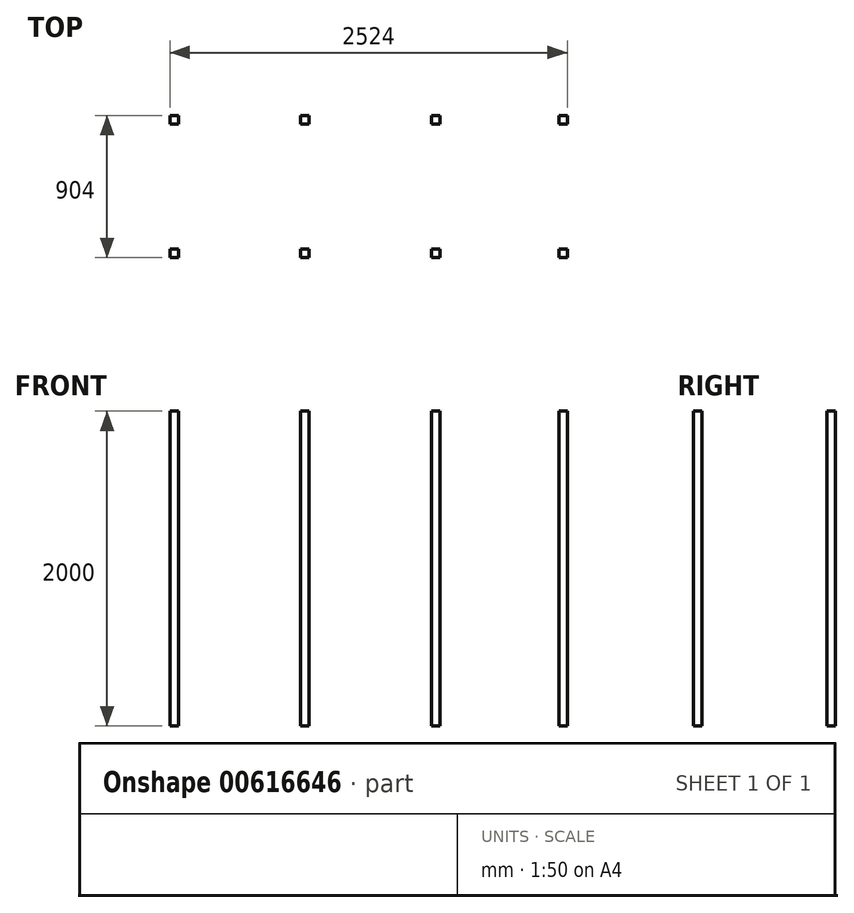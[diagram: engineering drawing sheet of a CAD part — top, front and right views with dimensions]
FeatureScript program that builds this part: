
annotation { "Feature Type Name" : "Feature", "Feature Type Description" : "" }
export const myFeature = defineFeature(function(context is Context, id is Id, definition is map)
    precondition{}
    {
        {
            var Q0;
            Q0=qCreatedBy(makeId("Front.planeOp"),FACE);
            var sketch = newSketch(context, id + "F0", { "sketchPlane" : qUnion([Q0])});
            skLineSegment(sketch, "E0.bottom", {"start": v(0, 2000) * mm, "end": v(54, 2000) * mm});
            skLineSegment(sketch, "E0.top", {"start": v(0, 0) * mm, "end": v(54, 0) * mm});
            skLineSegment(sketch, "E0.left", {"start": v(0, 2000) * mm, "end": v(0, 0) * mm});
            skLineSegment(sketch, "E0.right", {"start": v(54, 2000) * mm, "end": v(54, 0) * mm});
            skSolve(sketch);
        }
        {
            var Q0;
            Q0 = qSketchRegion(id + "F0", true);
            extrude(context, id + "F1", {"entities" : qUnion([Q0]), "depth" : 54 * mm, "offsetDistance" : 25 * mm});
        }
        {
            var Q0;
            Q0=makeQuery(id+"F1.opExtrude","SWEPT_BODY",BODY,{"disambiguationData":[OSD([sQuery(id+"F0.wireOp",EDGE,"E0.bottom"),sQuery(id+"F0.wireOp",EDGE,"E0.top"),sQuery(id+"F0.wireOp",EDGE,"E0.left"),sQuery(id+"F0.wireOp",EDGE,"E0.right")])]});
            transform(context, id + "F2", {"entities" : qUnion([Q0]), "transformType" : TransformType.TRANSLATION_3D, "dx" : 830 * mm, "dy" : 0 * mm, "dz" : 0 * mm, "makeCopy" : true});
        }
        {
            var Q0;
            Q0=makeQuery(id+"F2.opPattern","COPY",BODY,{"derivedFrom":makeQuery(id+"F1.opExtrude","SWEPT_BODY",BODY,{"disambiguationData":[OSD([sQuery(id+"F0.wireOp",EDGE,"E0.bottom"),sQuery(id+"F0.wireOp",EDGE,"E0.top"),sQuery(id+"F0.wireOp",EDGE,"E0.left"),sQuery(id+"F0.wireOp",EDGE,"E0.right")])]}),"instanceName":"1"});
            transform(context, id + "F3", {"entities" : qUnion([Q0]), "transformType" : TransformType.TRANSLATION_3D, "dx" : 830 * mm, "dy" : 0 * mm, "dz" : 0 * mm, "makeCopy" : true});
        }
        {
            var Q0;
            Q0=makeQuery(id+"F3.opPattern","COPY",BODY,{"derivedFrom":makeQuery(id+"F2.opPattern","COPY",BODY,{"derivedFrom":makeQuery(id+"F1.opExtrude","SWEPT_BODY",BODY,{"disambiguationData":[OSD([sQuery(id+"F0.wireOp",EDGE,"E0.bottom"),sQuery(id+"F0.wireOp",EDGE,"E0.top"),sQuery(id+"F0.wireOp",EDGE,"E0.left"),sQuery(id+"F0.wireOp",EDGE,"E0.right")])]}),"instanceName":"1"}),"instanceName":"1"});
            transform(context, id + "F4", {"entities" : qUnion([Q0]), "transformType" : TransformType.TRANSLATION_3D, "dx" : 810 * mm, "dy" : 0 * mm, "dz" : 0 * mm, "makeCopy" : true});
        }
        {
            var Q0;
            Q0=makeQuery(id+"F1.opExtrude","SWEPT_BODY",BODY,{"disambiguationData":[OSD([sQuery(id+"F0.wireOp",EDGE,"E0.bottom"),sQuery(id+"F0.wireOp",EDGE,"E0.top"),sQuery(id+"F0.wireOp",EDGE,"E0.left"),sQuery(id+"F0.wireOp",EDGE,"E0.right")])]});
            transform(context, id + "F5", {"entities" : qUnion([Q0]), "transformType" : TransformType.TRANSLATION_3D, "dx" : 0 * mm, "dy" : 730 * mm, "dz" : 0 * mm, "makeCopy" : true});
        }
        {
            var Q0;
            Q0=makeQuery(id+"F3.opPattern","COPY",BODY,{"derivedFrom":makeQuery(id+"F2.opPattern","COPY",BODY,{"derivedFrom":makeQuery(id+"F1.opExtrude","SWEPT_BODY",BODY,{"disambiguationData":[OSD([sQuery(id+"F0.wireOp",EDGE,"E0.bottom"),sQuery(id+"F0.wireOp",EDGE,"E0.top"),sQuery(id+"F0.wireOp",EDGE,"E0.left"),sQuery(id+"F0.wireOp",EDGE,"E0.right")])]}),"instanceName":"1"}),"instanceName":"1"});
            var Q1;
            Q1=makeQuery(id+"F2.opPattern","COPY",BODY,{"derivedFrom":makeQuery(id+"F1.opExtrude","SWEPT_BODY",BODY,{"disambiguationData":[OSD([sQuery(id+"F0.wireOp",EDGE,"E0.bottom"),sQuery(id+"F0.wireOp",EDGE,"E0.top"),sQuery(id+"F0.wireOp",EDGE,"E0.left"),sQuery(id+"F0.wireOp",EDGE,"E0.right")])]}),"instanceName":"1"});
            var Q2;
            Q2=makeQuery(id+"F4.opPattern","COPY",BODY,{"derivedFrom":makeQuery(id+"F3.opPattern","COPY",BODY,{"derivedFrom":makeQuery(id+"F2.opPattern","COPY",BODY,{"derivedFrom":makeQuery(id+"F1.opExtrude","SWEPT_BODY",BODY,{"disambiguationData":[OSD([sQuery(id+"F0.wireOp",EDGE,"E0.bottom"),sQuery(id+"F0.wireOp",EDGE,"E0.top"),sQuery(id+"F0.wireOp",EDGE,"E0.left"),sQuery(id+"F0.wireOp",EDGE,"E0.right")])]}),"instanceName":"1"}),"instanceName":"1"}),"instanceName":"1"});
            var Q3;
            Q3=makeQuery(id+"F1.opExtrude","SWEPT_BODY",BODY,{"disambiguationData":[OSD([sQuery(id+"F0.wireOp",EDGE,"E0.bottom"),sQuery(id+"F0.wireOp",EDGE,"E0.top"),sQuery(id+"F0.wireOp",EDGE,"E0.left"),sQuery(id+"F0.wireOp",EDGE,"E0.right")])]});
            transform(context, id + "F6", {"entities" : qUnion([Q0, Q1, Q2, Q3]), "transformType" : TransformType.TRANSLATION_3D, "dx" : 0 * mm, "dy" : 850 * mm, "dz" : 0 * mm, "makeCopy" : true});
        }
        {
            var Q0;
            Q0=makeQuery(id+"F5.opPattern","COPY",BODY,{"derivedFrom":makeQuery(id+"F1.opExtrude","SWEPT_BODY",BODY,{"disambiguationData":[OSD([sQuery(id+"F0.wireOp",EDGE,"E0.bottom"),sQuery(id+"F0.wireOp",EDGE,"E0.top"),sQuery(id+"F0.wireOp",EDGE,"E0.left"),sQuery(id+"F0.wireOp",EDGE,"E0.right")])]}),"instanceName":"1"});
            deleteBodies(context, id + "F7", {"entities" : qUnion([Q0])});
        }
    });
